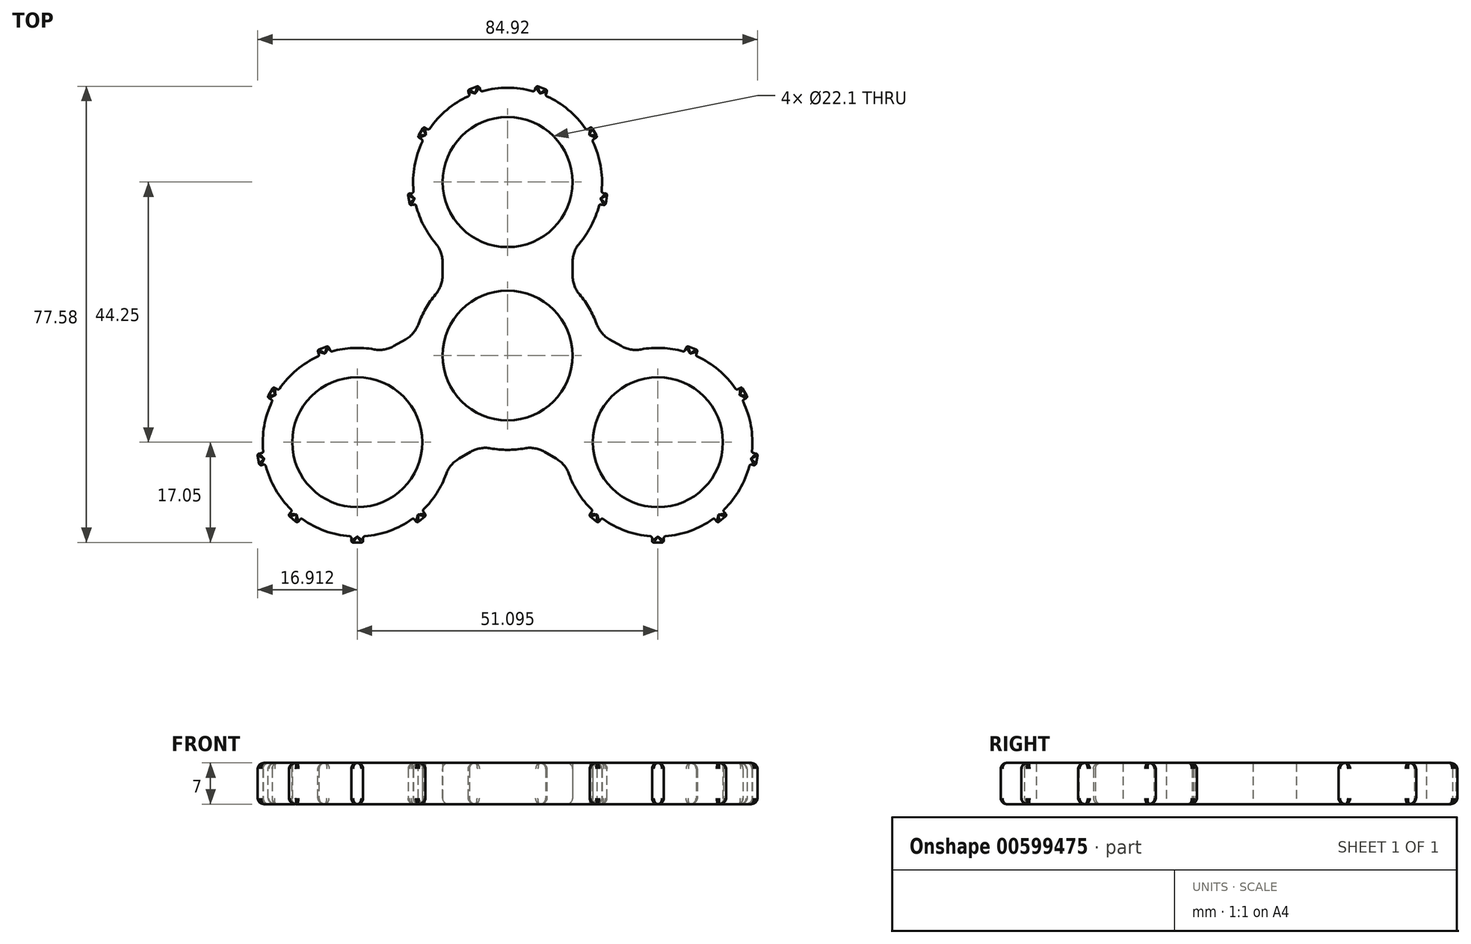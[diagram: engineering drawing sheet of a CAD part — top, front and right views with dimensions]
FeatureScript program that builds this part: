
annotation { "Feature Type Name" : "Feature", "Feature Type Description" : "" }
export const myFeature = defineFeature(function(context is Context, id is Id, definition is map)
    precondition{}
    {
        {
            var Q0;
            Q0=qCreatedBy(makeId("Top.planeOp"),FACE);
            var sketch = newSketch(context, id + "F0", { "sketchPlane" : qUnion([Q0])});
            skCircle(sketch, "E0", {"center": v(0, 0) * mm, "radius": 11.05 * mm});
            skLineSegment(sketch, "E1", {"start": v(0, 0) * mm, "end": v(0, 29.5) * mm, "construction": true});
            skCircle(sketch, "E2", {"center": v(0, 29.5) * mm, "radius": 11.05 * mm});
            skLineSegment(sketch, "E3", {"start": v(-11.05, 17.86) * mm, "end": v(-11.05, 11.64) * mm});
            skLineSegment(sketch, "E4", {"start": v(11.05, 17.86) * mm, "end": v(11.05, 11.64) * mm});
            skArc(sketch, "E5.0", {"start": v(-11.05, 11.64) * mm, "mid": v(0, -16.05) * mm, "end": v(11.05, 11.64) * mm});
            skArc(sketch, "E6.0", {"start": v(11.05, 17.86) * mm, "mid": v(13.9, 21.47) * mm, "end": v(15.6, 25.73) * mm});
            skArc(sketch, "E7", {"start": v(-11.05, 17.86) * mm, "mid": v(0, 13.45) * mm, "end": v(11.05, 17.86) * mm, "construction": true});
            skLineSegment(sketch, "E8.bottom", {"start": v(1, 12.45) * mm, "end": v(-1, 12.45) * mm, "construction": true});
            skLineSegment(sketch, "E8.top", {"start": v(1, 14.45) * mm, "end": v(-1, 14.45) * mm, "construction": true});
            skLineSegment(sketch, "E8.left", {"start": v(1, 12.45) * mm, "end": v(1, 14.45) * mm, "construction": true});
            skLineSegment(sketch, "E8.right", {"start": v(-1, 12.45) * mm, "end": v(-1, 14.45) * mm, "construction": true});
            skPoint(sketch, "E8.middle", {"position": v(0, 13.45) * mm});
            skLineSegment(sketch, "E9.2.0", {"start": v(-16.96, 27.52) * mm, "end": v(-15.95, 27.7) * mm});
            skLineSegment(sketch, "E9.2.2", {"start": v(-16.62, 25.55) * mm, "end": v(-15.6, 25.73) * mm});
            skLineSegment(sketch, "E9.2.3", {"start": v(-16.62, 25.55) * mm, "end": v(-16.96, 27.52) * mm});
            skLineSegment(sketch, "E9.3.0", {"start": v(-14.27, 38.9) * mm, "end": v(-13.37, 38.38) * mm});
            skLineSegment(sketch, "E9.3.2", {"start": v(-15.27, 37.16) * mm, "end": v(-14.37, 36.64) * mm});
            skLineSegment(sketch, "E9.3.3", {"start": v(-15.27, 37.16) * mm, "end": v(-14.27, 38.9) * mm});
            skLineSegment(sketch, "E9.4.0", {"start": v(-4.9, 45.86) * mm, "end": v(-4.54, 44.9) * mm});
            skLineSegment(sketch, "E9.4.2", {"start": v(-6.77, 45.18) * mm, "end": v(-6.42, 44.21) * mm});
            skLineSegment(sketch, "E9.4.3", {"start": v(-6.77, 45.18) * mm, "end": v(-4.9, 45.86) * mm});
            skLineSegment(sketch, "E9.5.0", {"start": v(6.77, 45.18) * mm, "end": v(6.42, 44.21) * mm});
            skLineSegment(sketch, "E9.5.2", {"start": v(4.9, 45.86) * mm, "end": v(4.54, 44.9) * mm});
            skLineSegment(sketch, "E9.5.3", {"start": v(4.9, 45.86) * mm, "end": v(6.77, 45.18) * mm});
            skLineSegment(sketch, "E9.6.0", {"start": v(15.27, 37.16) * mm, "end": v(14.37, 36.64) * mm});
            skLineSegment(sketch, "E9.6.2", {"start": v(14.27, 38.9) * mm, "end": v(13.37, 38.38) * mm});
            skLineSegment(sketch, "E9.6.3", {"start": v(14.27, 38.9) * mm, "end": v(15.27, 37.16) * mm});
            skLineSegment(sketch, "E9.7.0", {"start": v(16.62, 25.55) * mm, "end": v(15.6, 25.73) * mm});
            skLineSegment(sketch, "E9.7.2", {"start": v(16.96, 27.52) * mm, "end": v(15.95, 27.7) * mm});
            skLineSegment(sketch, "E9.7.3", {"start": v(16.96, 27.52) * mm, "end": v(16.62, 25.55) * mm});
            skLineSegment(sketch, "E9.anchor1", {"start": v(0, 29.5) * mm, "end": v(-1, 12.45) * mm, "construction": true});
            skLineSegment(sketch, "E9.anchor2", {"start": v(0, 29.5) * mm, "end": v(-1, 12.5) * mm, "construction": true});
            skArc(sketch, "E10.trimOffspring", {"start": v(15.95, 27.7) * mm, "mid": v(15.8, 32.29) * mm, "end": v(14.37, 36.64) * mm});
            skArc(sketch, "E11.trimOffspring", {"start": v(13.37, 38.38) * mm, "mid": v(10.32, 41.8) * mm, "end": v(6.42, 44.21) * mm});
            skArc(sketch, "E12.trimOffspring", {"start": v(4.54, 44.9) * mm, "mid": v(0, 45.55) * mm, "end": v(-4.54, 44.9) * mm});
            skArc(sketch, "E13.trimOffspring", {"start": v(-6.42, 44.21) * mm, "mid": v(-10.32, 41.8) * mm, "end": v(-13.37, 38.38) * mm});
            skArc(sketch, "E14.trimOffspring", {"start": v(-14.37, 36.64) * mm, "mid": v(-15.8, 32.29) * mm, "end": v(-15.95, 27.7) * mm});
            skArc(sketch, "E15.trimOffspring", {"start": v(-15.6, 25.73) * mm, "mid": v(-13.9, 21.47) * mm, "end": v(-11.05, 17.86) * mm});
            skSolve(sketch);
        }
        {
            var Q0;
            Q0=makeQuery(id+"F0.imprint","IMPRINT",FACE,{"disambiguationData":[TD([[makeQuery(id+"F0.imprint","IMPRINT",EDGE,{"derivedFrom":sQuery(id+"F0.wireOp",EDGE,"E0")}),-1.0]])]});
            extrude(context, id + "F1", {"entities" : qUnion([Q0]), "depth" : 7 * mm, "offsetDistance" : 25 * mm});
        }
        {
            var Q0;
            Q0=makeQuery(id+"F1.opExtrude","SWEPT_EDGE",EDGE,{"disambiguationData":[OSD([sQuery(id+"F0.wireOp",EDGE,"E3"),sQuery(id+"F0.wireOp",EDGE,"E5.0")])]});
            var Q1;
            Q1=makeQuery(id+"F1.opExtrude","SWEPT_EDGE",EDGE,{"disambiguationData":[OSD([sQuery(id+"F0.wireOp",EDGE,"E3"),sQuery(id+"F0.wireOp",EDGE,"E15.trimOffspring")])]});
            var Q2;
            Q2=makeQuery(id+"F1.opExtrude","SWEPT_EDGE",EDGE,{"disambiguationData":[OSD([sQuery(id+"F0.wireOp",EDGE,"E4"),sQuery(id+"F0.wireOp",EDGE,"E6.0")])]});
            var Q3;
            Q3=makeQuery(id+"F1.opExtrude","SWEPT_EDGE",EDGE,{"disambiguationData":[OSD([sQuery(id+"F0.wireOp",EDGE,"E4"),sQuery(id+"F0.wireOp",EDGE,"E5.0")])]});
            fillet(context, id + "F2", {"entities" : qUnion([Q0, Q1, Q2, Q3]), "radius" : 5 * mm, "tangentPropagation" : true, "allowEdgeOverflow" : false});
        }
        {
            var Q0;
            Q0=makeQuery(id+"F1.opExtrude","SWEPT_EDGE",EDGE,{"disambiguationData":[OSD([sQuery(id+"F0.wireOp",EDGE,"E9.2.2"),sQuery(id+"F0.wireOp",EDGE,"E15.trimOffspring")])]});
            var Q1;
            Q1=makeQuery(id+"F1.opExtrude","SWEPT_EDGE",EDGE,{"disambiguationData":[OSD([sQuery(id+"F0.wireOp",EDGE,"E9.2.2"),sQuery(id+"F0.wireOp",EDGE,"E9.2.3")])]});
            var Q2;
            Q2=makeQuery(id+"F1.opExtrude","SWEPT_EDGE",EDGE,{"disambiguationData":[OSD([sQuery(id+"F0.wireOp",EDGE,"E9.2.0"),sQuery(id+"F0.wireOp",EDGE,"E9.2.3")])]});
            var Q3;
            Q3=makeQuery(id+"F1.opExtrude","SWEPT_EDGE",EDGE,{"disambiguationData":[OSD([sQuery(id+"F0.wireOp",EDGE,"E9.2.0"),sQuery(id+"F0.wireOp",EDGE,"E14.trimOffspring")])]});
            var Q4;
            Q4=makeQuery(id+"F1.opExtrude","SWEPT_EDGE",EDGE,{"disambiguationData":[OSD([sQuery(id+"F0.wireOp",EDGE,"E9.3.2"),sQuery(id+"F0.wireOp",EDGE,"E14.trimOffspring")])]});
            var Q5;
            Q5=makeQuery(id+"F1.opExtrude","SWEPT_EDGE",EDGE,{"disambiguationData":[OSD([sQuery(id+"F0.wireOp",EDGE,"E9.3.2"),sQuery(id+"F0.wireOp",EDGE,"E9.3.3")])]});
            var Q6;
            Q6=makeQuery(id+"F1.opExtrude","SWEPT_EDGE",EDGE,{"disambiguationData":[OSD([sQuery(id+"F0.wireOp",EDGE,"E9.3.0"),sQuery(id+"F0.wireOp",EDGE,"E9.3.3")])]});
            var Q7;
            Q7=makeQuery(id+"F1.opExtrude","SWEPT_EDGE",EDGE,{"disambiguationData":[OSD([sQuery(id+"F0.wireOp",EDGE,"E9.3.0"),sQuery(id+"F0.wireOp",EDGE,"E13.trimOffspring")])]});
            var Q8;
            Q8=makeQuery(id+"F1.opExtrude","SWEPT_EDGE",EDGE,{"disambiguationData":[OSD([sQuery(id+"F0.wireOp",EDGE,"E9.4.2"),sQuery(id+"F0.wireOp",EDGE,"E13.trimOffspring")])]});
            var Q9;
            Q9=makeQuery(id+"F1.opExtrude","SWEPT_EDGE",EDGE,{"disambiguationData":[OSD([sQuery(id+"F0.wireOp",EDGE,"E9.4.2"),sQuery(id+"F0.wireOp",EDGE,"E9.4.3")])]});
            var Q10;
            Q10=makeQuery(id+"F1.opExtrude","SWEPT_EDGE",EDGE,{"disambiguationData":[OSD([sQuery(id+"F0.wireOp",EDGE,"E9.4.0"),sQuery(id+"F0.wireOp",EDGE,"E9.4.3")])]});
            var Q11;
            Q11=makeQuery(id+"F1.opExtrude","SWEPT_EDGE",EDGE,{"disambiguationData":[OSD([sQuery(id+"F0.wireOp",EDGE,"E9.4.0"),sQuery(id+"F0.wireOp",EDGE,"E12.trimOffspring")])]});
            var Q12;
            Q12=makeQuery(id+"F1.opExtrude","SWEPT_EDGE",EDGE,{"disambiguationData":[OSD([sQuery(id+"F0.wireOp",EDGE,"E9.5.2"),sQuery(id+"F0.wireOp",EDGE,"E12.trimOffspring")])]});
            var Q13;
            Q13=makeQuery(id+"F1.opExtrude","SWEPT_EDGE",EDGE,{"disambiguationData":[OSD([sQuery(id+"F0.wireOp",EDGE,"E9.5.2"),sQuery(id+"F0.wireOp",EDGE,"E9.5.3")])]});
            var Q14;
            Q14=makeQuery(id+"F1.opExtrude","SWEPT_EDGE",EDGE,{"disambiguationData":[OSD([sQuery(id+"F0.wireOp",EDGE,"E9.5.0"),sQuery(id+"F0.wireOp",EDGE,"E9.5.3")])]});
            var Q15;
            Q15=makeQuery(id+"F1.opExtrude","SWEPT_EDGE",EDGE,{"disambiguationData":[OSD([sQuery(id+"F0.wireOp",EDGE,"E9.5.0"),sQuery(id+"F0.wireOp",EDGE,"E11.trimOffspring")])]});
            var Q16;
            Q16=makeQuery(id+"F1.opExtrude","SWEPT_EDGE",EDGE,{"disambiguationData":[OSD([sQuery(id+"F0.wireOp",EDGE,"E9.6.2"),sQuery(id+"F0.wireOp",EDGE,"E11.trimOffspring")])]});
            var Q17;
            Q17=makeQuery(id+"F1.opExtrude","SWEPT_EDGE",EDGE,{"disambiguationData":[OSD([sQuery(id+"F0.wireOp",EDGE,"E9.6.2"),sQuery(id+"F0.wireOp",EDGE,"E9.6.3")])]});
            var Q18;
            Q18=makeQuery(id+"F1.opExtrude","SWEPT_EDGE",EDGE,{"disambiguationData":[OSD([sQuery(id+"F0.wireOp",EDGE,"E9.6.0"),sQuery(id+"F0.wireOp",EDGE,"E9.6.3")])]});
            var Q19;
            Q19=makeQuery(id+"F1.opExtrude","SWEPT_EDGE",EDGE,{"disambiguationData":[OSD([sQuery(id+"F0.wireOp",EDGE,"E9.6.0"),sQuery(id+"F0.wireOp",EDGE,"E10.trimOffspring")])]});
            var Q20;
            Q20=makeQuery(id+"F1.opExtrude","SWEPT_EDGE",EDGE,{"disambiguationData":[OSD([sQuery(id+"F0.wireOp",EDGE,"E9.7.2"),sQuery(id+"F0.wireOp",EDGE,"E10.trimOffspring")])]});
            var Q21;
            Q21=makeQuery(id+"F1.opExtrude","SWEPT_EDGE",EDGE,{"disambiguationData":[OSD([sQuery(id+"F0.wireOp",EDGE,"E9.7.2"),sQuery(id+"F0.wireOp",EDGE,"E9.7.3")])]});
            var Q22;
            Q22=makeQuery(id+"F1.opExtrude","SWEPT_EDGE",EDGE,{"disambiguationData":[OSD([sQuery(id+"F0.wireOp",EDGE,"E9.7.0"),sQuery(id+"F0.wireOp",EDGE,"E9.7.3")])]});
            var Q23;
            Q23=makeQuery(id+"F1.opExtrude","SWEPT_EDGE",EDGE,{"disambiguationData":[OSD([sQuery(id+"F0.wireOp",EDGE,"E6.0"),sQuery(id+"F0.wireOp",EDGE,"E9.7.0")])]});
            fillet(context, id + "F3", {"entities" : qUnion([Q0, Q1, Q2, Q3, Q4, Q5, Q6, Q7, Q8, Q9, Q10, Q11, Q12, Q13, Q14, Q15, Q16, Q17, Q18, Q19, Q20, Q21, Q22, Q23]), "radius" : 0.3 * mm, "tangentPropagation" : true, "allowEdgeOverflow" : false});
        }
        {
            var Q0;
            Q0=qCreatedBy(makeId("Right.planeOp"),FACE);
            var sketch = newSketch(context, id + "F4", { "sketchPlane" : qUnion([Q0])});
            skLineSegment(sketch, "E16", {"start": v(0, 28.22) * mm, "end": v(0, -30.36) * mm, "construction": true});
            skSolve(sketch);
        }
        {
            var Q0;
            Q0=makeQuery(id+"F1.opExtrude","SWEPT_BODY",BODY,{"disambiguationData":[OSD([sQuery(id+"F0.wireOp",EDGE,"E0"),sQuery(id+"F0.wireOp",EDGE,"E2"),sQuery(id+"F0.wireOp",EDGE,"E3"),sQuery(id+"F0.wireOp",EDGE,"E4"),sQuery(id+"F0.wireOp",EDGE,"E5.0"),sQuery(id+"F0.wireOp",EDGE,"E6.0"),sQuery(id+"F0.wireOp",EDGE,"E9.2.0"),sQuery(id+"F0.wireOp",EDGE,"E9.2.2"),sQuery(id+"F0.wireOp",EDGE,"E9.2.3"),sQuery(id+"F0.wireOp",EDGE,"E9.3.0"),sQuery(id+"F0.wireOp",EDGE,"E9.3.2"),sQuery(id+"F0.wireOp",EDGE,"E9.3.3"),sQuery(id+"F0.wireOp",EDGE,"E9.4.0"),sQuery(id+"F0.wireOp",EDGE,"E9.4.2"),sQuery(id+"F0.wireOp",EDGE,"E9.4.3"),sQuery(id+"F0.wireOp",EDGE,"E9.5.0"),sQuery(id+"F0.wireOp",EDGE,"E9.5.2"),sQuery(id+"F0.wireOp",EDGE,"E9.5.3"),sQuery(id+"F0.wireOp",EDGE,"E9.6.0"),sQuery(id+"F0.wireOp",EDGE,"E9.6.2"),sQuery(id+"F0.wireOp",EDGE,"E9.6.3"),sQuery(id+"F0.wireOp",EDGE,"E9.7.0"),sQuery(id+"F0.wireOp",EDGE,"E9.7.2"),sQuery(id+"F0.wireOp",EDGE,"E9.7.3"),sQuery(id+"F0.wireOp",EDGE,"E10.trimOffspring"),sQuery(id+"F0.wireOp",EDGE,"E11.trimOffspring"),sQuery(id+"F0.wireOp",EDGE,"E12.trimOffspring"),sQuery(id+"F0.wireOp",EDGE,"E13.trimOffspring"),sQuery(id+"F0.wireOp",EDGE,"E14.trimOffspring"),sQuery(id+"F0.wireOp",EDGE,"E15.trimOffspring")])]});
            var Q1;
            Q1=sQuery(id+"F4.wireOp",EDGE,"E16");
            circularPattern(context, id + "F5", {"operationType" : NewBodyOperationType.ADD, "entities" : qUnion([Q0]), "axis" : qUnion([Q1]), "angle" : 360 * degree, "instanceCount" : 3, "equalSpace" : true});
        }
        {
            var Q0;
            Q0=makeQuery(id+"F5.opPattern","COPY",EDGE,{"derivedFrom":makeQuery(id+"F1.opExtrude","CAP_EDGE",EDGE,{"disambiguationData":[OSD([sQuery(id+"F0.wireOp",EDGE,"E3")])],"isStart":true}),"instanceName":"2"});
            var Q1;
            Q1=makeQuery(id+"F5.opPattern","COPY",EDGE,{"derivedFrom":makeQuery(id+"F1.opExtrude","CAP_EDGE",EDGE,{"disambiguationData":[OSD([sQuery(id+"F0.wireOp",EDGE,"E3")])],"isStart":false}),"instanceName":"2"});
            fillet(context, id + "F6", {"entities" : qUnion([Q0, Q1]), "radius" : 1 * mm, "tangentPropagation" : true, "allowEdgeOverflow" : false});
        }
    });
